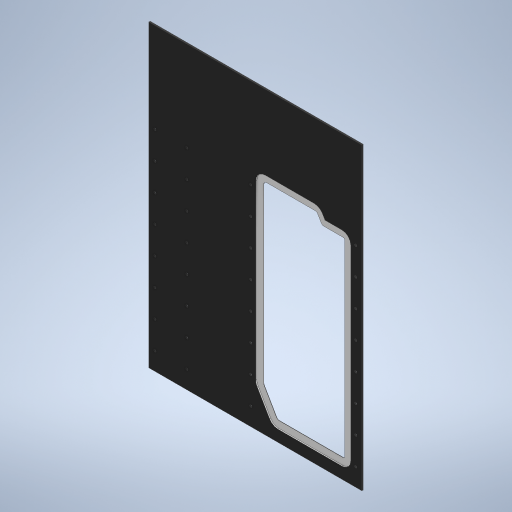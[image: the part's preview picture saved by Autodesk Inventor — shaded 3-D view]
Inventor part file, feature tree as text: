
AUTODESK INVENTOR PART (.ipt)
format: ipt  version: 2024 (Build 280153000, 153)  size: 380,928 bytes
history: native  units: mm
features: other x5, fillet x3, projected_geometry x3, extrude x2, sketch x2
ambient origin geometry x8: Origin, YZ Plane, XZ Plane, XY Plane, X Axis, Y Axis, Z Axis, Center Point
bodies: Body1 (feature_tree)
feature tree (15):
  other  "Side Panel.ipt"
  extrude  "Extrusion1"  Depth=20.0mm
  fillet  "Fillet1"  Radius=20.0mm
  fillet  "Fillet2"  Radius=16.0mm
  fillet  "Fillet3"  Radius=16.0mm
  extrude  "Extrusion2"  TaperAngle=120.0deg  [1 undecoded]
  other  "Cladding::Side Panel.ipt"
  other  "TaggingFeature1"
  sketch  "Sketch1"  dims[d0=10.0mm d1=20.0mm d4=20.0mm d5=16.0mm d6=16.0mm]
  projected_geometry  "Projected Loop1"
  sketch  "Sketch2"  dims[d7=40.0mm d8=120.0deg d9=30.0mm d10=50.0mm d11=40.0mm d12=2.38125mm d13=0.0mm d14=6.0mm d15=6.0mm d16=4.0mm d17=15.0mm d18=2.38125mm d19=0.0mm d20=39.0mm d21=39.0mm]
  projected_geometry  "Projected Loop2"
  projected_geometry  "Projected Loop3"
  other  "Cladding"
  other  "Core"
note: 1 required parameter value undecoded (feature->parameter linkage not recoverable at this tier; creation-order binding heuristic only, values carry confidence <= 0.55)
